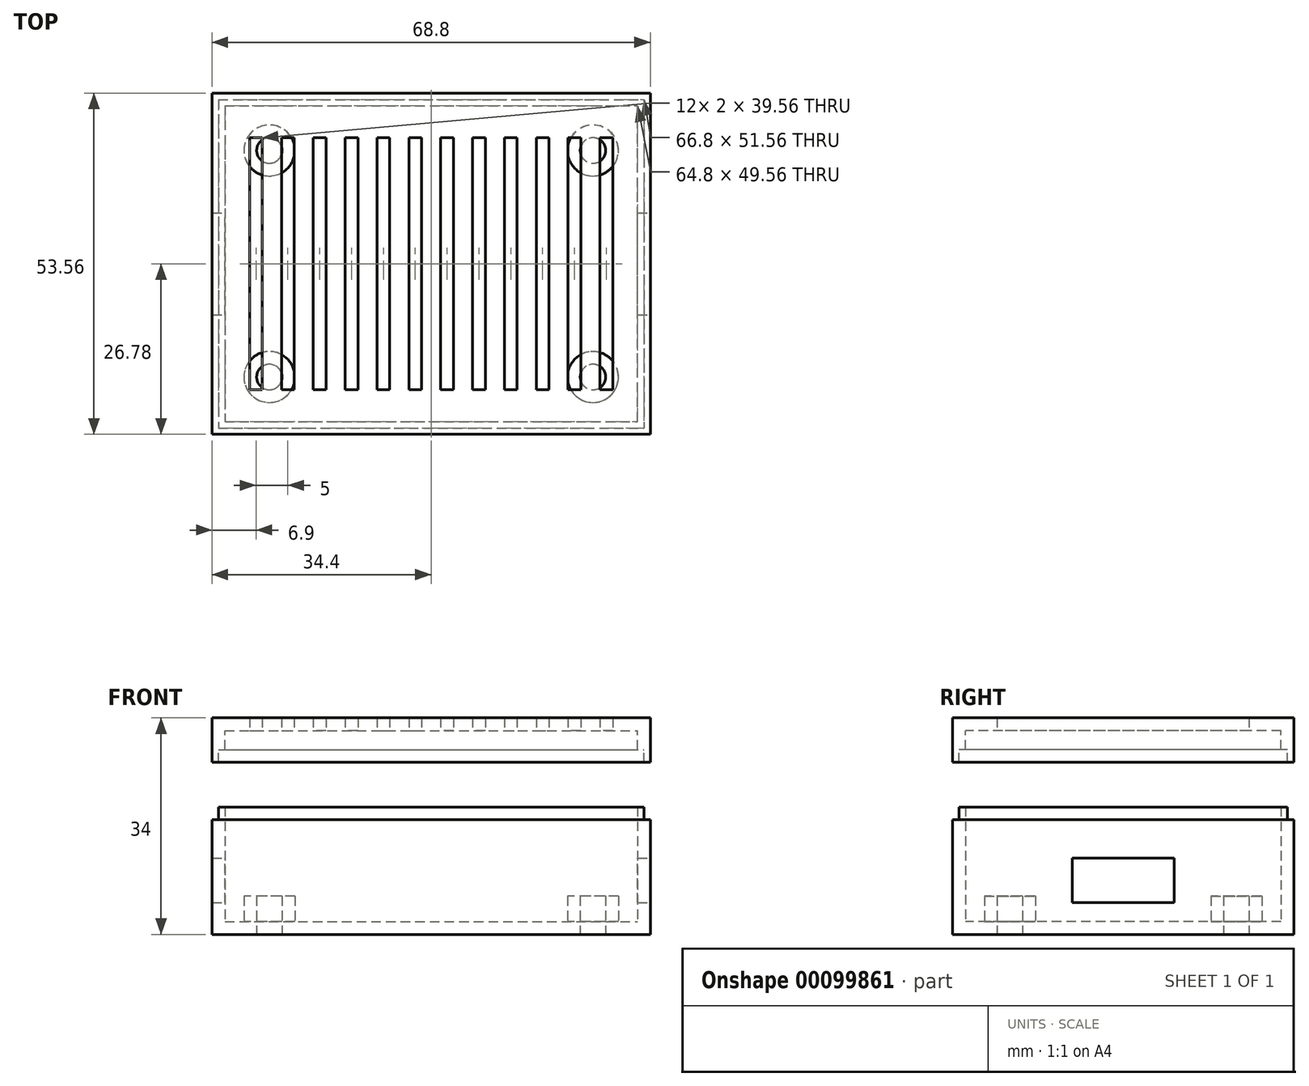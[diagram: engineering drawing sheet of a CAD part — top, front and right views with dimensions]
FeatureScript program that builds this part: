
annotation { "Feature Type Name" : "Feature", "Feature Type Description" : "" }
export const myFeature = defineFeature(function(context is Context, id is Id, definition is map)
    precondition{}
    {
        {
            var Q0;
            Q0=qCreatedBy(makeId("Top.planeOp"),FACE);
            var sketch = newSketch(context, id + "F0", { "sketchPlane" : qUnion([Q0])});
            skLineSegment(sketch, "E0.bottom", {"start": v(-32.4, 24.78) * mm, "end": v(32.4, 24.78) * mm});
            skLineSegment(sketch, "E0.top", {"start": v(-32.4, -24.78) * mm, "end": v(32.4, -24.78) * mm});
            skLineSegment(sketch, "E0.left", {"start": v(-32.4, 24.78) * mm, "end": v(-32.4, -24.78) * mm});
            skLineSegment(sketch, "E0.right", {"start": v(32.4, 24.78) * mm, "end": v(32.4, -24.78) * mm});
            skPoint(sketch, "E0.middle", {"position": v(0, 0) * mm});
            skCircle(sketch, "E1", {"center": v(-25.4, 17.78) * mm, "radius": 4 * mm});
            skCircle(sketch, "E2", {"center": v(-25.4, -17.78) * mm, "radius": 4 * mm});
            skCircle(sketch, "E3", {"center": v(-25.4, 17.78) * mm, "radius": 2 * mm});
            skCircle(sketch, "E4", {"center": v(25.4, 17.78) * mm, "radius": 4 * mm});
            skCircle(sketch, "E5.MirrorC", {"center": v(-25.4, -17.78) * mm, "radius": 2 * mm});
            skCircle(sketch, "E6.MirrorC", {"center": v(25.4, 17.78) * mm, "radius": 2 * mm});
            skCircle(sketch, "E7.MirrorC", {"center": v(25.4, -17.78) * mm, "radius": 2 * mm});
            skCircle(sketch, "E8.MirrorC", {"center": v(25.4, -17.78) * mm, "radius": 4 * mm});
            skLineSegment(sketch, "E9.bottom", {"start": v(-34.4, 26.78) * mm, "end": v(34.4, 26.78) * mm});
            skLineSegment(sketch, "E9.top", {"start": v(-34.4, -26.78) * mm, "end": v(34.4, -26.78) * mm});
            skLineSegment(sketch, "E9.left", {"start": v(-34.4, 26.78) * mm, "end": v(-34.4, -26.78) * mm});
            skLineSegment(sketch, "E9.right", {"start": v(34.4, 26.78) * mm, "end": v(34.4, -26.78) * mm});
            skSolve(sketch);
        }
        {
            var Q0;
            Q0=makeQuery(id+"F0.imprint","IMPRINT",FACE,{"disambiguationData":[TD([[makeQuery(id+"F0.imprint","IMPRINT",EDGE,{"derivedFrom":sQuery(id+"F0.wireOp",EDGE,"E0.bottom")}),-1.0]])]});
            extrude(context, id + "F1", {"entities" : qUnion([Q0]), "depth" : 2 * mm});
        }
        {
            var Q0;
            Q0=makeQuery(id+"F0.imprint","IMPRINT",FACE,{"disambiguationData":[TD([[makeQuery(id+"F0.imprint","IMPRINT",EDGE,{"derivedFrom":sQuery(id+"F0.wireOp",EDGE,"E1")}),1.0]])]});
            var Q1;
            Q1=makeQuery(id+"F0.imprint","IMPRINT",FACE,{"disambiguationData":[TD([[makeQuery(id+"F0.imprint","IMPRINT",EDGE,{"derivedFrom":sQuery(id+"F0.wireOp",EDGE,"E4")}),1.0]])]});
            var Q2;
            Q2=makeQuery(id+"F0.imprint","IMPRINT",FACE,{"disambiguationData":[TD([[makeQuery(id+"F0.imprint","IMPRINT",EDGE,{"derivedFrom":sQuery(id+"F0.wireOp",EDGE,"E7.MirrorC")}),-1.0]])]});
            var Q3;
            Q3=makeQuery(id+"F0.imprint","IMPRINT",FACE,{"disambiguationData":[TD([[makeQuery(id+"F0.imprint","IMPRINT",EDGE,{"derivedFrom":sQuery(id+"F0.wireOp",EDGE,"E2")}),1.0]])]});
            extrude(context, id + "F2", {"entities" : qUnion([Q0, Q1, Q2, Q3]), "operationType" : NewBodyOperationType.ADD, "depth" : 6 * mm});
        }
        {
            var Q0;
            Q0=makeQuery(id+"F0.imprint","IMPRINT",FACE,{"disambiguationData":[TD([[makeQuery(id+"F0.imprint","IMPRINT",EDGE,{"derivedFrom":sQuery(id+"F0.wireOp",EDGE,"E3")}),1.0]])]});
            var Q1;
            Q1=makeQuery(id+"F0.imprint","IMPRINT",FACE,{"disambiguationData":[TD([[makeQuery(id+"F0.imprint","IMPRINT",EDGE,{"derivedFrom":sQuery(id+"F0.wireOp",EDGE,"E5.MirrorC")}),-1.0]])]});
            var Q2;
            Q2=makeQuery(id+"F0.imprint","IMPRINT",FACE,{"disambiguationData":[TD([[makeQuery(id+"F0.imprint","IMPRINT",EDGE,{"derivedFrom":sQuery(id+"F0.wireOp",EDGE,"E7.MirrorC")}),1.0]])]});
            var Q3;
            Q3=makeQuery(id+"F0.imprint","IMPRINT",FACE,{"disambiguationData":[TD([[makeQuery(id+"F0.imprint","IMPRINT",EDGE,{"derivedFrom":sQuery(id+"F0.wireOp",EDGE,"E6.MirrorC")}),-1.0]])]});
            extrude(context, id + "F3", {"entities" : qUnion([Q0, Q1, Q2, Q3]), "operationType" : NewBodyOperationType.ADD, "depth" : 2 * mm});
        }
        {
            var Q0;
            Q0=makeQuery(id+"F0.imprint","IMPRINT",FACE,{"disambiguationData":[TD([[makeQuery(id+"F0.imprint","IMPRINT",EDGE,{"derivedFrom":sQuery(id+"F0.wireOp",EDGE,"E0.bottom")}),1.0]])]});
            extrude(context, id + "F4", {"entities" : qUnion([Q0]), "operationType" : NewBodyOperationType.ADD, "depth" : 20 * mm});
        }
        {
            var Q0;
            Q0=makeQuery(id+"F4.opExtrude","CAP_FACE",FACE,{"disambiguationData":[OSD([sQuery(id+"F0.wireOp",EDGE,"E0.bottom"),sQuery(id+"F0.wireOp",EDGE,"E0.top"),sQuery(id+"F0.wireOp",EDGE,"E0.left"),sQuery(id+"F0.wireOp",EDGE,"E0.right"),sQuery(id+"F0.wireOp",EDGE,"E9.bottom"),sQuery(id+"F0.wireOp",EDGE,"E9.top"),sQuery(id+"F0.wireOp",EDGE,"E9.left"),sQuery(id+"F0.wireOp",EDGE,"E9.right")])],"isStart":false});
            var sketch = newSketch(context, id + "F5", { "sketchPlane" : qUnion([Q0])});
            skLineSegment(sketch, "E10.bottom", {"start": v(-33.4, 25.78) * mm, "end": v(33.4, 25.78) * mm});
            skLineSegment(sketch, "E10.top", {"start": v(-33.4, -25.78) * mm, "end": v(33.4, -25.78) * mm});
            skLineSegment(sketch, "E10.left", {"start": v(-33.4, 25.78) * mm, "end": v(-33.4, -25.78) * mm});
            skLineSegment(sketch, "E10.right", {"start": v(33.4, 25.78) * mm, "end": v(33.4, -25.78) * mm});
            skPoint(sketch, "E10.middle", {"position": v(0, 0) * mm});
            skLineSegment(sketch, "E11.0.0", {"start": v(32.4, 24.78) * mm, "end": v(-32.4, 24.78) * mm});
            skLineSegment(sketch, "E11.0.1", {"start": v(-32.4, 24.78) * mm, "end": v(-32.4, -24.78) * mm});
            skLineSegment(sketch, "E11.0.2", {"start": v(-32.4, -24.78) * mm, "end": v(32.4, -24.78) * mm});
            skLineSegment(sketch, "E11.0.3", {"start": v(32.4, -24.78) * mm, "end": v(32.4, 24.78) * mm});
            skLineSegment(sketch, "E12.0", {"start": v(-34.4, 26.78) * mm, "end": v(-34.4, -26.78) * mm});
            skLineSegment(sketch, "E13.0", {"start": v(-34.4, 26.78) * mm, "end": v(34.4, 26.78) * mm});
            skLineSegment(sketch, "E14.0", {"start": v(-34.4, -26.78) * mm, "end": v(34.4, -26.78) * mm});
            skLineSegment(sketch, "E15.0", {"start": v(34.4, 26.78) * mm, "end": v(34.4, -26.78) * mm});
            skSolve(sketch);
        }
        {
            var Q0;
            Q0=qSketchRegion(id+"F5",true);
            extrude(context, id + "F6", {"entities" : qUnion([Q0]), "operationType" : NewBodyOperationType.REMOVE, "oppositeDirection" : true, "depth" : 2 * mm});
        }
        {
            var Q0;
            Q0=qCreatedBy(makeId("Right.planeOp"),FACE);
            var sketch = newSketch(context, id + "F7", { "sketchPlane" : qUnion([Q0])});
            skLineSegment(sketch, "E16.bottom", {"start": v(-8, 5) * mm, "end": v(8, 5) * mm});
            skLineSegment(sketch, "E16.top", {"start": v(-8, 12) * mm, "end": v(8, 12) * mm});
            skLineSegment(sketch, "E16.left", {"start": v(-8, 5) * mm, "end": v(-8, 12) * mm});
            skLineSegment(sketch, "E16.right", {"start": v(8, 5) * mm, "end": v(8, 12) * mm});
            skSolve(sketch);
        }
        {
            var Q0;
            Q0=qSketchRegion(id+"F7",true);
            extrude(context, id + "F8", {"entities" : qUnion([Q0]), "operationType" : NewBodyOperationType.REMOVE, "oppositeDirection" : true, "depth" : 40 * mm, "hasSecondDirection" : true, "secondDirectionOppositeDirection" : false, "secondDirectionDepth" : 40 * mm});
        }
        {
            var Q0;
            Q0=makeQuery(id+"F4.opExtrude","CAP_FACE",FACE,{"disambiguationData":[OSD([sQuery(id+"F0.wireOp",EDGE,"E0.bottom"),sQuery(id+"F0.wireOp",EDGE,"E0.top"),sQuery(id+"F0.wireOp",EDGE,"E0.left"),sQuery(id+"F0.wireOp",EDGE,"E0.right"),sQuery(id+"F0.wireOp",EDGE,"E9.bottom"),sQuery(id+"F0.wireOp",EDGE,"E9.top"),sQuery(id+"F0.wireOp",EDGE,"E9.left"),sQuery(id+"F0.wireOp",EDGE,"E9.right")])],"isStart":false});
            cPlane(context, id + "F9", {"entities" : qUnion([Q0]), "cplaneType" : CPlaneType.OFFSET, "offset" : 12 * mm, "width" : 150 * mm, "height" : 150 * mm});
        }
        {
            var Q0;
            Q0=qCreatedBy(id+"F9.planeOp",FACE);
            var sketch = newSketch(context, id + "F10", { "sketchPlane" : qUnion([Q0])});
            skLineSegment(sketch, "E17.left", {"start": v(-28.5, 19.78) * mm, "end": v(-28.5, -19.78) * mm});
            skLineSegment(sketch, "E18", {"start": v(-28.5, 19.78) * mm, "end": v(-26.5, 19.78) * mm});
            skLineSegment(sketch, "E19", {"start": v(-26.5, 19.78) * mm, "end": v(-26.5, -19.78) * mm});
            skLineSegment(sketch, "E20", {"start": v(-28.5, -19.78) * mm, "end": v(-26.5, -19.78) * mm});
            skLineSegment(sketch, "E21.left", {"start": v(-23.5, 19.78) * mm, "end": v(-23.5, -19.78) * mm});
            skLineSegment(sketch, "E22", {"start": v(-23.5, 19.78) * mm, "end": v(-21.5, 19.78) * mm});
            skLineSegment(sketch, "E23", {"start": v(-21.5, 19.78) * mm, "end": v(-21.5, -19.78) * mm});
            skLineSegment(sketch, "E24", {"start": v(-23.5, -19.78) * mm, "end": v(-21.5, -19.78) * mm});
            skLineSegment(sketch, "E25", {"start": v(-20, 22.94) * mm, "end": v(-20, -17.5) * mm, "construction": true});
            skLineSegment(sketch, "E26.MirrorCS", {"start": v(-11.5, 19.78) * mm, "end": v(-13.5, 19.78) * mm});
            skLineSegment(sketch, "E27.MirrorCS", {"start": v(-11.5, 19.78) * mm, "end": v(-11.5, -19.78) * mm});
            skLineSegment(sketch, "E28.MirrorCS", {"start": v(-13.5, 19.78) * mm, "end": v(-13.5, -19.78) * mm});
            skLineSegment(sketch, "E29.MirrorCS", {"start": v(-16.5, 19.78) * mm, "end": v(-16.5, -19.78) * mm});
            skLineSegment(sketch, "E30.MirrorCS", {"start": v(-16.5, 19.78) * mm, "end": v(-18.5, 19.78) * mm});
            skLineSegment(sketch, "E31.MirrorCS", {"start": v(-16.5, -19.78) * mm, "end": v(-18.5, -19.78) * mm});
            skLineSegment(sketch, "E32.MirrorCS", {"start": v(-11.5, -19.78) * mm, "end": v(-13.5, -19.78) * mm});
            skLineSegment(sketch, "E33.MirrorCS", {"start": v(-18.5, 19.78) * mm, "end": v(-18.5, -19.78) * mm});
            skLineSegment(sketch, "E34", {"start": v(-10, 21.68) * mm, "end": v(-10, -19.6) * mm, "construction": true});
            skLineSegment(sketch, "E35.MirrorCS", {"start": v(-3.5, 19.78) * mm, "end": v(-1.5, 19.78) * mm});
            skLineSegment(sketch, "E36.MirrorCS", {"start": v(-6.5, 19.78) * mm, "end": v(-6.5, -19.78) * mm});
            skLineSegment(sketch, "E37.MirrorCS", {"start": v(-3.5, 19.78) * mm, "end": v(-3.5, -19.78) * mm});
            skLineSegment(sketch, "E38.MirrorCS", {"start": v(-3.5, -19.78) * mm, "end": v(-1.5, -19.78) * mm});
            skLineSegment(sketch, "E39.MirrorCS", {"start": v(-8.5, -19.78) * mm, "end": v(-6.5, -19.78) * mm});
            skLineSegment(sketch, "E40.MirrorCS", {"start": v(-8.5, 19.78) * mm, "end": v(-8.5, -19.78) * mm});
            skLineSegment(sketch, "E41.MirrorCS", {"start": v(-8.5, 19.78) * mm, "end": v(-6.5, 19.78) * mm});
            skLineSegment(sketch, "E42.MirrorCS", {"start": v(-1.5, 19.78) * mm, "end": v(-1.5, -19.78) * mm});
            skLineSegment(sketch, "E43", {"start": v(0, 21.5) * mm, "end": v(0, -15.9) * mm, "construction": true});
            skLineSegment(sketch, "E44.MirrorCS", {"start": v(23.5, -19.78) * mm, "end": v(21.5, -19.78) * mm});
            skLineSegment(sketch, "E45.MirrorCS", {"start": v(8.5, -19.78) * mm, "end": v(6.5, -19.78) * mm});
            skLineSegment(sketch, "E46.MirrorCS", {"start": v(20, 22.94) * mm, "end": v(20, -17.5) * mm, "construction": true});
            skLineSegment(sketch, "E47.MirrorCS", {"start": v(13.5, 19.78) * mm, "end": v(13.5, -19.78) * mm});
            skLineSegment(sketch, "E48.MirrorCS", {"start": v(16.5, 19.78) * mm, "end": v(16.5, -19.78) * mm});
            skLineSegment(sketch, "E49.MirrorCS", {"start": v(28.5, -19.78) * mm, "end": v(26.5, -19.78) * mm});
            skLineSegment(sketch, "E50.MirrorCS", {"start": v(26.5, 19.78) * mm, "end": v(26.5, -19.78) * mm});
            skLineSegment(sketch, "E51.MirrorCS", {"start": v(28.5, 19.78) * mm, "end": v(26.5, 19.78) * mm});
            skLineSegment(sketch, "E52.MirrorCS", {"start": v(11.5, 19.78) * mm, "end": v(11.5, -19.78) * mm});
            skLineSegment(sketch, "E53.MirrorCS", {"start": v(18.5, 19.78) * mm, "end": v(18.5, -19.78) * mm});
            skLineSegment(sketch, "E54.MirrorCS", {"start": v(28.5, 19.78) * mm, "end": v(28.5, -19.78) * mm});
            skLineSegment(sketch, "E55.MirrorCS", {"start": v(11.5, -19.78) * mm, "end": v(13.5, -19.78) * mm});
            skLineSegment(sketch, "E56.MirrorCS", {"start": v(16.5, -19.78) * mm, "end": v(18.5, -19.78) * mm});
            skLineSegment(sketch, "E57.MirrorCS", {"start": v(1.5, 19.78) * mm, "end": v(1.5, -19.78) * mm});
            skLineSegment(sketch, "E58.MirrorCS", {"start": v(3.5, 19.78) * mm, "end": v(1.5, 19.78) * mm});
            skLineSegment(sketch, "E59.MirrorCS", {"start": v(3.5, 19.78) * mm, "end": v(3.5, -19.78) * mm});
            skLineSegment(sketch, "E60.MirrorCS", {"start": v(21.5, 19.78) * mm, "end": v(21.5, -19.78) * mm});
            skLineSegment(sketch, "E61.MirrorCS", {"start": v(6.5, 19.78) * mm, "end": v(6.5, -19.78) * mm});
            skLineSegment(sketch, "E62.MirrorCS", {"start": v(10, 21.68) * mm, "end": v(10, -19.6) * mm, "construction": true});
            skLineSegment(sketch, "E63.MirrorCS", {"start": v(8.5, 19.78) * mm, "end": v(6.5, 19.78) * mm});
            skLineSegment(sketch, "E64.MirrorCS", {"start": v(23.5, 19.78) * mm, "end": v(21.5, 19.78) * mm});
            skLineSegment(sketch, "E65.MirrorCS", {"start": v(3.5, -19.78) * mm, "end": v(1.5, -19.78) * mm});
            skLineSegment(sketch, "E66.MirrorCS", {"start": v(8.5, 19.78) * mm, "end": v(8.5, -19.78) * mm});
            skLineSegment(sketch, "E67.MirrorCS", {"start": v(23.5, 19.78) * mm, "end": v(23.5, -19.78) * mm});
            skLineSegment(sketch, "E68.MirrorCS", {"start": v(11.5, 19.78) * mm, "end": v(13.5, 19.78) * mm});
            skLineSegment(sketch, "E69.MirrorCS", {"start": v(16.5, 19.78) * mm, "end": v(18.5, 19.78) * mm});
            skLineSegment(sketch, "E70.0", {"start": v(-32.4, -24.78) * mm, "end": v(32.4, -24.78) * mm});
            skLineSegment(sketch, "E71.0", {"start": v(-32.4, 24.78) * mm, "end": v(-32.4, -24.78) * mm});
            skLineSegment(sketch, "E72.0", {"start": v(-32.4, 24.78) * mm, "end": v(32.4, 24.78) * mm});
            skLineSegment(sketch, "E73", {"start": v(32.4, -24.78) * mm, "end": v(32.4, 24.78) * mm});
            skLineSegment(sketch, "E74.0", {"start": v(-34.4, 26.78) * mm, "end": v(34.4, 26.78) * mm});
            skLineSegment(sketch, "E75.0", {"start": v(-34.4, 26.78) * mm, "end": v(-34.4, -26.78) * mm});
            skLineSegment(sketch, "E76.0", {"start": v(34.4, 26.78) * mm, "end": v(34.4, -26.78) * mm});
            skLineSegment(sketch, "E77.0", {"start": v(-34.4, -26.78) * mm, "end": v(34.4, -26.78) * mm});
            skLineSegment(sketch, "E78.0", {"start": v(-33.4, 25.78) * mm, "end": v(33.4, 25.78) * mm});
            skLineSegment(sketch, "E79.0", {"start": v(-33.4, 25.78) * mm, "end": v(-33.4, -25.78) * mm});
            skLineSegment(sketch, "E80.0", {"start": v(33.4, 25.78) * mm, "end": v(33.4, -25.78) * mm});
            skLineSegment(sketch, "E81.0", {"start": v(-33.4, -25.78) * mm, "end": v(33.4, -25.78) * mm});
            skSolve(sketch);
        }
        {
            var Q0;
            Q0=qSketchRegion(id+"F10",true);
            var Q1;
            Q1=makeQuery(id+"F10.imprint","IMPRINT",FACE,{"disambiguationData":[TD([[makeQuery(id+"F10.imprint","IMPRINT",EDGE,{"derivedFrom":sQuery(id+"F10.wireOp",EDGE,"E17.left")}),-1.0]])]});
            var Q2;
            Q2=makeQuery(id+"F10.imprint","IMPRINT",FACE,{"disambiguationData":[TD([[makeQuery(id+"F10.imprint","IMPRINT",EDGE,{"derivedFrom":sQuery(id+"F10.wireOp",EDGE,"E70.0")}),-1.0]])]});
            extrude(context, id + "F11", {"entities" : qUnion([Q0, Q1, Q2]), "depth" : 2 * mm});
        }
        {
            var Q0;
            Q0=qSketchRegion(id+"F10",true);
            extrude(context, id + "F12", {"entities" : qUnion([Q0]), "operationType" : NewBodyOperationType.ADD, "oppositeDirection" : true, "depth" : 5 * mm});
        }
        {
            var Q0;
            Q0=makeQuery(id+"F10.imprint","IMPRINT",FACE,{"disambiguationData":[TD([[makeQuery(id+"F10.imprint","IMPRINT",EDGE,{"derivedFrom":sQuery(id+"F10.wireOp",EDGE,"E70.0")}),-1.0]])]});
            extrude(context, id + "F13", {"entities" : qUnion([Q0]), "operationType" : NewBodyOperationType.ADD, "oppositeDirection" : true, "depth" : 3 * mm});
        }
    });
